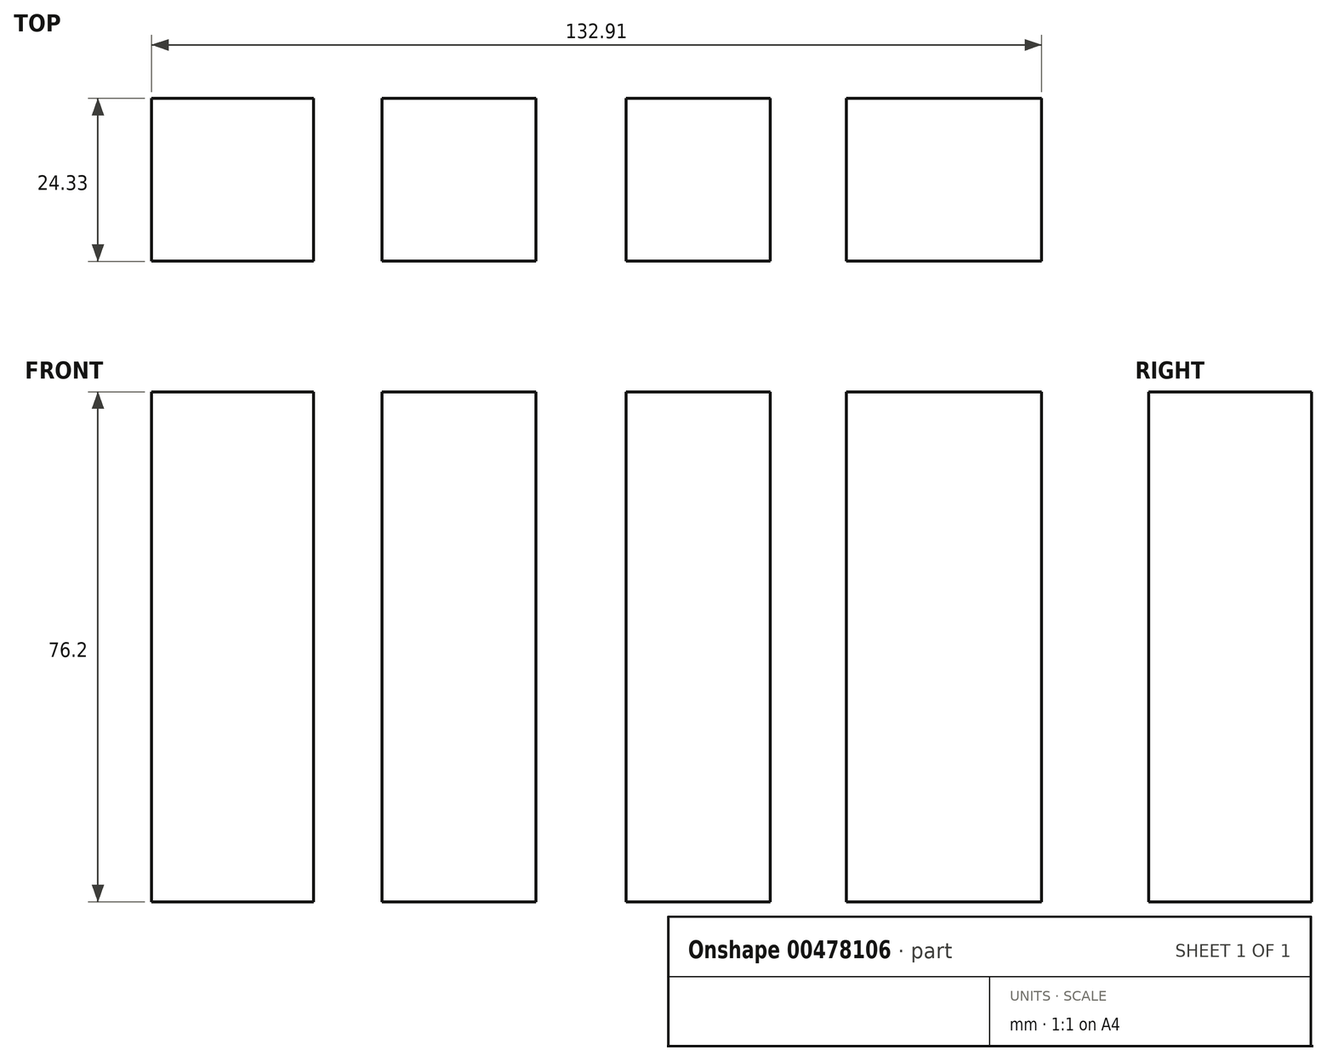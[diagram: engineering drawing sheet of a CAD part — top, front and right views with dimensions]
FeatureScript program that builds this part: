
annotation { "Feature Type Name" : "Feature", "Feature Type Description" : "" }
export const myFeature = defineFeature(function(context is Context, id is Id, definition is map)
    precondition{}
    {
        {
            var Q0;
            Q0=qCreatedBy(makeId("Top.planeOp"),FACE);
            var sketch = newSketch(context, id + "F0", { "sketchPlane" : qUnion([Q0])});
            skLineSegment(sketch, "E0.bottom", {"start": v(-70.83, 65.34) * mm, "end": v(-46.64, 65.34) * mm});
            skLineSegment(sketch, "E0.top", {"start": v(-70.83, 41.01) * mm, "end": v(-46.64, 41.01) * mm});
            skLineSegment(sketch, "E0.left", {"start": v(-70.83, 65.34) * mm, "end": v(-70.83, 41.01) * mm});
            skLineSegment(sketch, "E0.right", {"start": v(-46.64, 65.34) * mm, "end": v(-46.64, 41.01) * mm});
            skLineSegment(sketch, "E1.bottom", {"start": v(-36.43, 65.34) * mm, "end": v(-13.4, 65.34) * mm});
            skLineSegment(sketch, "E1.top", {"start": v(-36.43, 41.01) * mm, "end": v(-13.4, 41.01) * mm});
            skLineSegment(sketch, "E1.left", {"start": v(-36.43, 65.34) * mm, "end": v(-36.43, 41.01) * mm});
            skLineSegment(sketch, "E1.right", {"start": v(-13.4, 65.34) * mm, "end": v(-13.4, 41.01) * mm});
            skLineSegment(sketch, "E2.bottom", {"start": v(0, 41.01) * mm, "end": v(21.57, 41.01) * mm});
            skLineSegment(sketch, "E2.top", {"start": v(0, 65.34) * mm, "end": v(21.57, 65.34) * mm});
            skLineSegment(sketch, "E2.left", {"start": v(0, 41.01) * mm, "end": v(0, 65.34) * mm});
            skLineSegment(sketch, "E2.right", {"start": v(21.57, 41.01) * mm, "end": v(21.57, 65.34) * mm});
            skLineSegment(sketch, "E3.bottom", {"start": v(32.94, 65.34) * mm, "end": v(62.08, 65.34) * mm});
            skLineSegment(sketch, "E3.top", {"start": v(32.94, 41.01) * mm, "end": v(62.08, 41.01) * mm});
            skLineSegment(sketch, "E3.left", {"start": v(32.94, 65.34) * mm, "end": v(32.94, 41.01) * mm});
            skLineSegment(sketch, "E3.right", {"start": v(62.08, 65.34) * mm, "end": v(62.08, 41.01) * mm});
            skSolve(sketch);
        }
        {
            var Q0;
            Q0=makeQuery(id+"F0.imprint","IMPRINT",FACE,{"disambiguationData":[TD([[makeQuery(id+"F0.imprint","IMPRINT",EDGE,{"derivedFrom":sQuery(id+"F0.wireOp",EDGE,"E0.bottom")}),-1.0]])]});
            var Q1;
            Q1=makeQuery(id+"F0.imprint","IMPRINT",FACE,{"disambiguationData":[TD([[makeQuery(id+"F0.imprint","IMPRINT",EDGE,{"derivedFrom":sQuery(id+"F0.wireOp",EDGE,"E1.bottom")}),-1.0]])]});
            var Q2;
            Q2=makeQuery(id+"F0.imprint","IMPRINT",FACE,{"disambiguationData":[TD([[makeQuery(id+"F0.imprint","IMPRINT",EDGE,{"derivedFrom":sQuery(id+"F0.wireOp",EDGE,"E2.bottom")}),1.0]])]});
            var Q3;
            Q3=makeQuery(id+"F0.imprint","IMPRINT",FACE,{"disambiguationData":[TD([[makeQuery(id+"F0.imprint","IMPRINT",EDGE,{"derivedFrom":sQuery(id+"F0.wireOp",EDGE,"E3.bottom")}),-1.0]])]});
            extrude(context, id + "F1", {"entities" : qUnion([Q0, Q1, Q2, Q3]), "depth" : 76.2 * mm});
        }
    });
